# Revit family: STL22470BR_30_STL22470PTO_30
name_source: partatom
category: Luminárias
units: mm (PartAtom-declared; Revit-internal decimal feet)

## family parameters
Com base no plano de trabalho = Não
Compartilhado = Não
Corte com vazios quando carregada = Não
Cota do conector redondo = Utilizar diâmetro
Fonte luminosa = Sim
Manter orientação da anotação = Não
Ponto de cálculo do ambiente = Não
Sempre na vertical = Sim
Tipo de parte = Normal

## types (2) — shared parameters
Altura = 0.05 m
Comprimento = 0.33 m
Cromado = Cromado
Dimerização = Não dimerizável
Fabricante = Stella
Filtro de cor = 16777215
Fluxo Luminoso = 640 lm
Grau de proteção (IP) = IP20
IRC (Índice de reprodução de cores) = >93 (R9>60)
Largura = 0.04 m
Luminoso = Luminoso - 3000K
Modelo = Trace - Luminária de Luz Angular
Potência máxima = 13 W
Temperatura da cor (K) = 3000 K
Tensão Elétrica = 100V-240V
Troca de temperatura da cor de lâmpada com esmaecimento = <Nenhum>
URL = https://stella.com.br
Ângulo de Abertura = 80°
Ângulo de inclinação = 90.00°
zero-valued in all types: Elevação padrão

## per-type parameters (varying)
| type | Arquivo de rede fotométrica | Estrutura | Parafuso Branco | Parafuso Preto | Referência |
| STL22470BR/30 - BIVOLT - 3000K - 640lm - 80° | STELLA - STL22470BR-30 - TRACE 12,5W - LUMINÁRIA DE LUZ ANGULAR.ies | Al - Branco | Sim | Não | STL22470BR - BIVOLT |
| STL22470PTO/30 - BIVOLT - 3000K - 640lm - 80° | STELLA - STL22470PTO-30 - TRACE 12,5W - LUMINÁRIA DE LUZ ANGULAR.ies | Al - Preto | Não | Sim | STL22470PTO/30 - BIVOLT |
